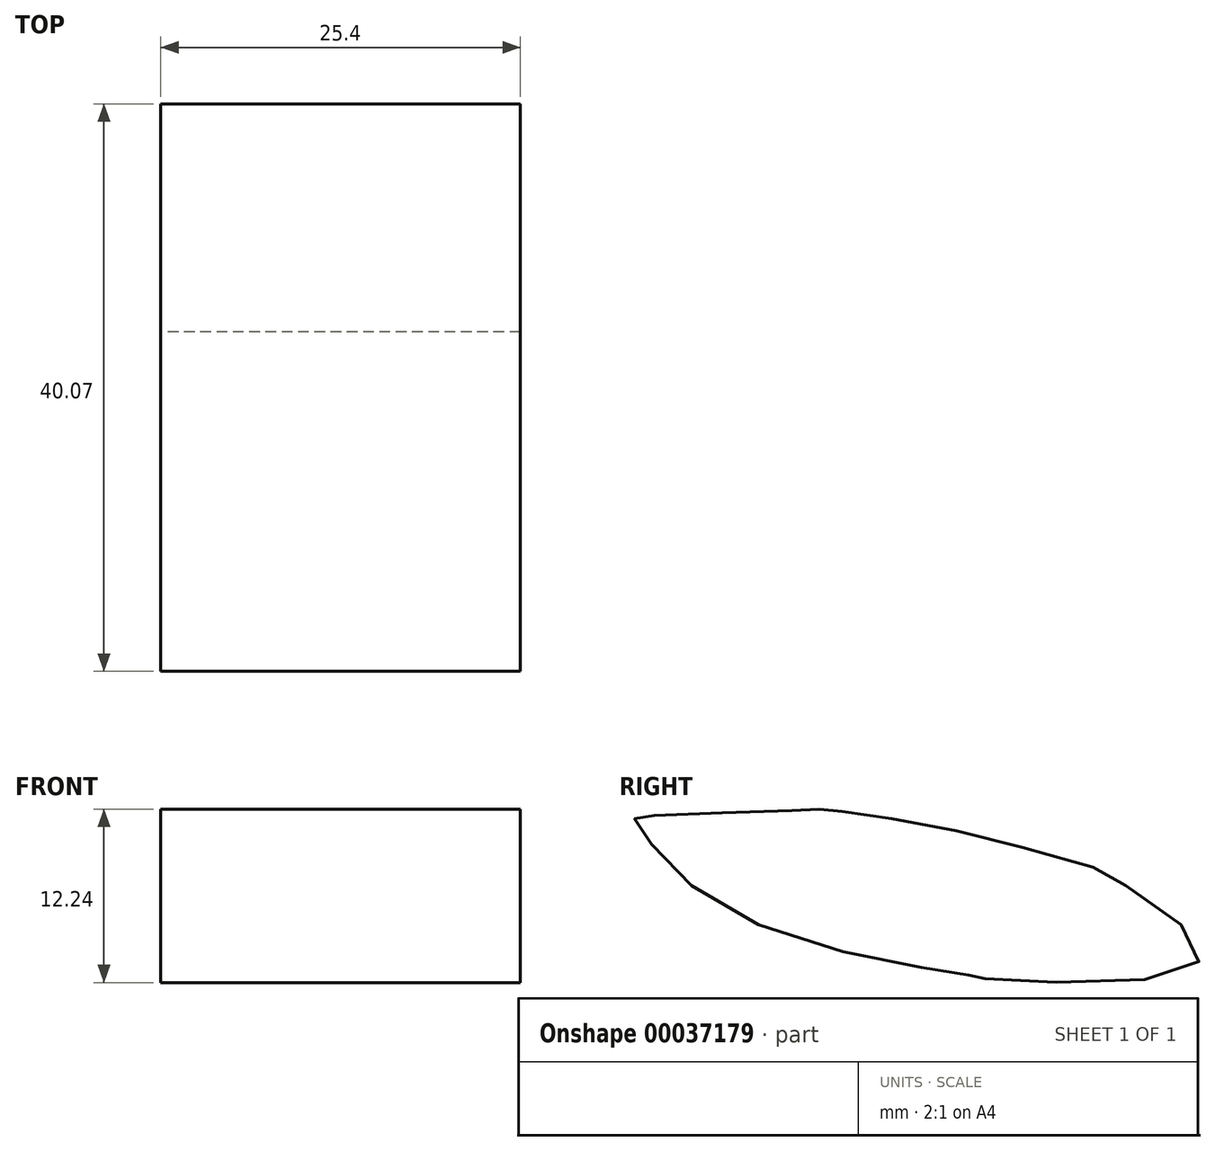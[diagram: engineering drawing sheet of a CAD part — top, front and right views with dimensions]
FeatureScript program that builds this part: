
annotation { "Feature Type Name" : "Feature", "Feature Type Description" : "" }
export const myFeature = defineFeature(function(context is Context, id is Id, definition is map)
    precondition{}
    {
        {
            var Q0;
            Q0=qCreatedBy(makeId("Right.planeOp"),FACE);
            var sketch = newSketch(context, id + "F0", { "sketchPlane" : qUnion([Q0])});
            skFitSpline(sketch, "E0", {"points": [v(-1.17, 5.58) * mm, v(8.43, 3.01) * mm, v(8.52, 2.99) * mm, v(16.04, -3.5) * mm, v(0, -4.73) * mm, v(0, -4.7) * mm, v(-17.38, 0) * mm, v(-23.96, 6.51) * mm, v(-23.96, 6.55) * mm, v(-11.36, 7.08) * mm, v(-10.7, 7.09) * mm, v(-1.17, 5.58) * mm]});
            skSolve(sketch);
        }
        {
            var Q0;
            Q0 = qSketchRegion(id + "F0", true);
            extrude(context, id + "F1", {"entities" : qUnion([Q0]), "depth" : 25.4 * mm});
        }
    });
